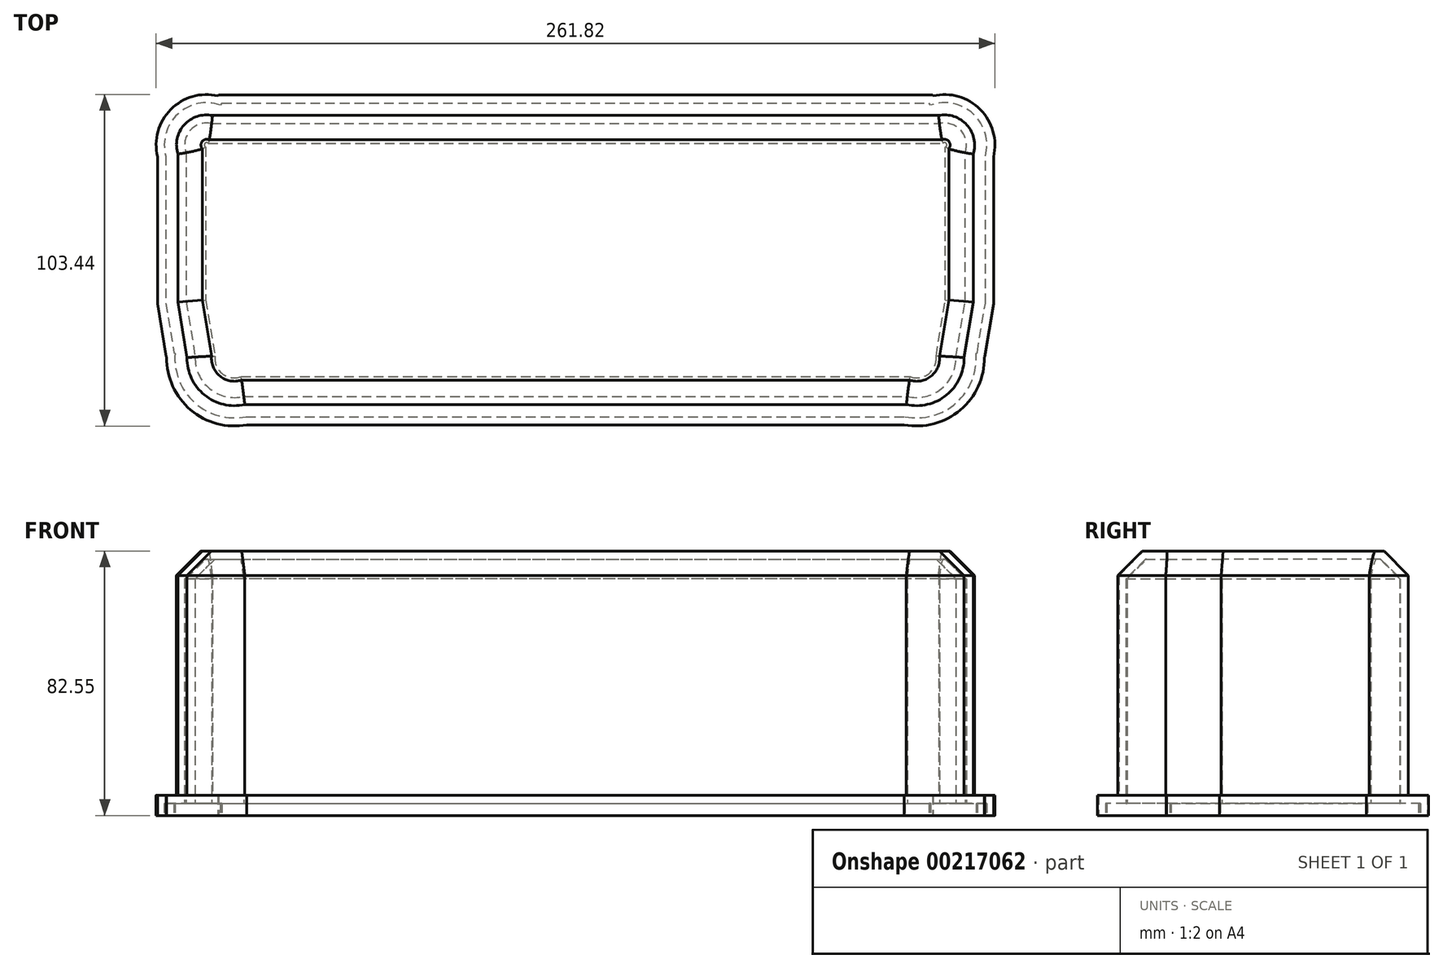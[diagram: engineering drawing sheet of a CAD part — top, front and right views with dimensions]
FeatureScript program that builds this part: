
annotation { "Feature Type Name" : "Feature", "Feature Type Description" : "" }
export const myFeature = defineFeature(function(context is Context, id is Id, definition is map)
    precondition{}
    {
        {
            var Q0;
            Q0=qCreatedBy(makeId("Top.planeOp"),FACE);
            var sketch = newSketch(context, id + "F0", { "sketchPlane" : qUnion([Q0])});
            skLineSegment(sketch, "E0", {"start": v(-17, -101.28) * mm, "end": v(205.83, -101.28) * mm});
            skLineSegment(sketch, "E1", {"start": v(-17, -101.28) * mm, "end": v(-17.23, -101.5) * mm});
            skLineSegment(sketch, "E2", {"start": v(-36.06, -120.33) * mm, "end": v(-36.06, -166.4) * mm});
            skLineSegment(sketch, "E3", {"start": v(-36.06, -166.4) * mm, "end": v(-33.34, -182.92) * mm});
            skLineSegment(sketch, "E4", {"start": v(-33.34, -182.92) * mm, "end": v(-33.2, -183.03) * mm});
            skLineSegment(sketch, "E5", {"start": v(-8.27, -204.19) * mm, "end": v(197.1, -204.19) * mm});
            skLineSegment(sketch, "E6", {"start": v(222.03, -183.03) * mm, "end": v(222.16, -182.92) * mm});
            skLineSegment(sketch, "E7", {"start": v(222.16, -182.92) * mm, "end": v(224.88, -166.4) * mm});
            skLineSegment(sketch, "E8", {"start": v(224.88, -166.4) * mm, "end": v(224.88, -120.33) * mm});
            skLineSegment(sketch, "E9", {"start": v(206.05, -101.5) * mm, "end": v(205.83, -101.28) * mm});
            skArc(sketch, "E10", {"start": v(-33.2, -183.03) * mm, "mid": v(-25.73, -199.54) * mm, "end": v(-8.22, -204.19) * mm});
            skArc(sketch, "E11", {"start": v(-17.23, -101.5) * mm, "mid": v(-31.95, -105.77) * mm, "end": v(-36.06, -120.53) * mm});
            skArc(sketch, "E12.MirrorC", {"start": v(206.05, -101.5) * mm, "mid": v(220.77, -105.77) * mm, "end": v(224.88, -120.53) * mm});
            skArc(sketch, "E13.MirrorC", {"start": v(222.03, -183.03) * mm, "mid": v(214.55, -199.54) * mm, "end": v(197.04, -204.19) * mm});
            skPoint(sketch, "E14.start.orphan", {"position": v(94.41, -101.28) * mm});
            skSolve(sketch);
        }
        {
            var Q0;
            Q0 = qSketchRegion(id + "F0", true);
            extrude(context, id + "F1", {"entities" : qUnion([Q0]), "depth" : 6.35 * mm});
        }
        {
            var Q0;
            Q0=makeQuery(id+"F1.opExtrude","CAP_FACE",FACE,{"disambiguationData":[OSD([sQuery(id+"F0.wireOp",EDGE,"E0"),sQuery(id+"F0.wireOp",EDGE,"E1"),sQuery(id+"F0.wireOp",EDGE,"E2"),sQuery(id+"F0.wireOp",EDGE,"E3"),sQuery(id+"F0.wireOp",EDGE,"E4"),sQuery(id+"F0.wireOp",EDGE,"E5"),sQuery(id+"F0.wireOp",EDGE,"E6"),sQuery(id+"F0.wireOp",EDGE,"E7"),sQuery(id+"F0.wireOp",EDGE,"E8"),sQuery(id+"F0.wireOp",EDGE,"E9"),sQuery(id+"F0.wireOp",EDGE,"E10"),sQuery(id+"F0.wireOp",EDGE,"E11"),sQuery(id+"F0.wireOp",EDGE,"E12.MirrorC"),sQuery(id+"F0.wireOp",EDGE,"E13.MirrorC")])],"isStart":false});
            var sketch = newSketch(context, id + "F2", { "sketchPlane" : qUnion([Q0])});
            skLineSegment(sketch, "E15.0", {"start": v(-18.91, -107.63) * mm, "end": v(207.74, -107.63) * mm});
            skArc(sketch, "E16.0", {"start": v(-18.91, -107.63) * mm, "mid": v(-27.75, -110.57) * mm, "end": v(-29.7, -119.68) * mm});
            skLineSegment(sketch, "E17.0", {"start": v(-29.7, -165.88) * mm, "end": v(-26.86, -183.2) * mm});
            skLineSegment(sketch, "E17.1", {"start": v(-29.7, -119.68) * mm, "end": v(-29.7, -165.88) * mm});
            skArc(sketch, "E18.0", {"start": v(-26.86, -183.2) * mm, "mid": v(-21.4, -194.88) * mm, "end": v(-8.85, -197.84) * mm});
            skLineSegment(sketch, "E19.0", {"start": v(-8.85, -197.84) * mm, "end": v(197.67, -197.84) * mm});
            skArc(sketch, "E20.0", {"start": v(215.68, -183.2) * mm, "mid": v(210.22, -194.88) * mm, "end": v(197.67, -197.84) * mm});
            skArc(sketch, "E21.0", {"start": v(207.74, -107.63) * mm, "mid": v(216.58, -110.57) * mm, "end": v(218.53, -119.68) * mm});
            skLineSegment(sketch, "E21.1", {"start": v(218.53, -165.88) * mm, "end": v(218.53, -119.68) * mm});
            skLineSegment(sketch, "E21.2", {"start": v(215.68, -183.2) * mm, "end": v(218.53, -165.88) * mm});
            skSolve(sketch);
        }
        {
            var Q0;
            Q0=makeQuery(id+"F2.imprint","IMPRINT",FACE,{"disambiguationData":[TD([[makeQuery(id+"F2.imprint","IMPRINT",EDGE,{"derivedFrom":sQuery(id+"F2.wireOp",EDGE,"E15.0")}),-1.0]])]});
            extrude(context, id + "F3", {"entities" : qUnion([Q0]), "operationType" : NewBodyOperationType.ADD, "depth" : 76.2 * mm});
        }
        {
            var Q0;
            Q0=makeQuery(id+"F3.opExtrude","CAP_FACE",FACE,{"disambiguationData":[OSD([sQuery(id+"F2.wireOp",EDGE,"E15.0"),sQuery(id+"F2.wireOp",EDGE,"E16.0"),sQuery(id+"F2.wireOp",EDGE,"E17.0"),sQuery(id+"F2.wireOp",EDGE,"E17.1"),sQuery(id+"F2.wireOp",EDGE,"E18.0"),sQuery(id+"F2.wireOp",EDGE,"E19.0"),sQuery(id+"F2.wireOp",EDGE,"E20.0"),sQuery(id+"F2.wireOp",EDGE,"E21.0"),sQuery(id+"F2.wireOp",EDGE,"E21.1"),sQuery(id+"F2.wireOp",EDGE,"E21.2")])],"isStart":false});
            chamfer(context, id + "F4", {"entities" : qUnion([Q0]), "width" : 7.62 * mm, "tangentPropagation" : true});
        }
        {
            var Q0;
            Q0=makeQuery(id+"F1.opExtrude","CAP_FACE",FACE,{"disambiguationData":[OSD([sQuery(id+"F0.wireOp",EDGE,"E0"),sQuery(id+"F0.wireOp",EDGE,"E1"),sQuery(id+"F0.wireOp",EDGE,"E2"),sQuery(id+"F0.wireOp",EDGE,"E3"),sQuery(id+"F0.wireOp",EDGE,"E4"),sQuery(id+"F0.wireOp",EDGE,"E5"),sQuery(id+"F0.wireOp",EDGE,"E6"),sQuery(id+"F0.wireOp",EDGE,"E7"),sQuery(id+"F0.wireOp",EDGE,"E8"),sQuery(id+"F0.wireOp",EDGE,"E9"),sQuery(id+"F0.wireOp",EDGE,"E10"),sQuery(id+"F0.wireOp",EDGE,"E11"),sQuery(id+"F0.wireOp",EDGE,"E12.MirrorC"),sQuery(id+"F0.wireOp",EDGE,"E13.MirrorC")])],"isStart":true});
            shell(context, id + "F5", {"entities" : qUnion([Q0]), "thickness" : 2.54 * mm});
        }
    });
